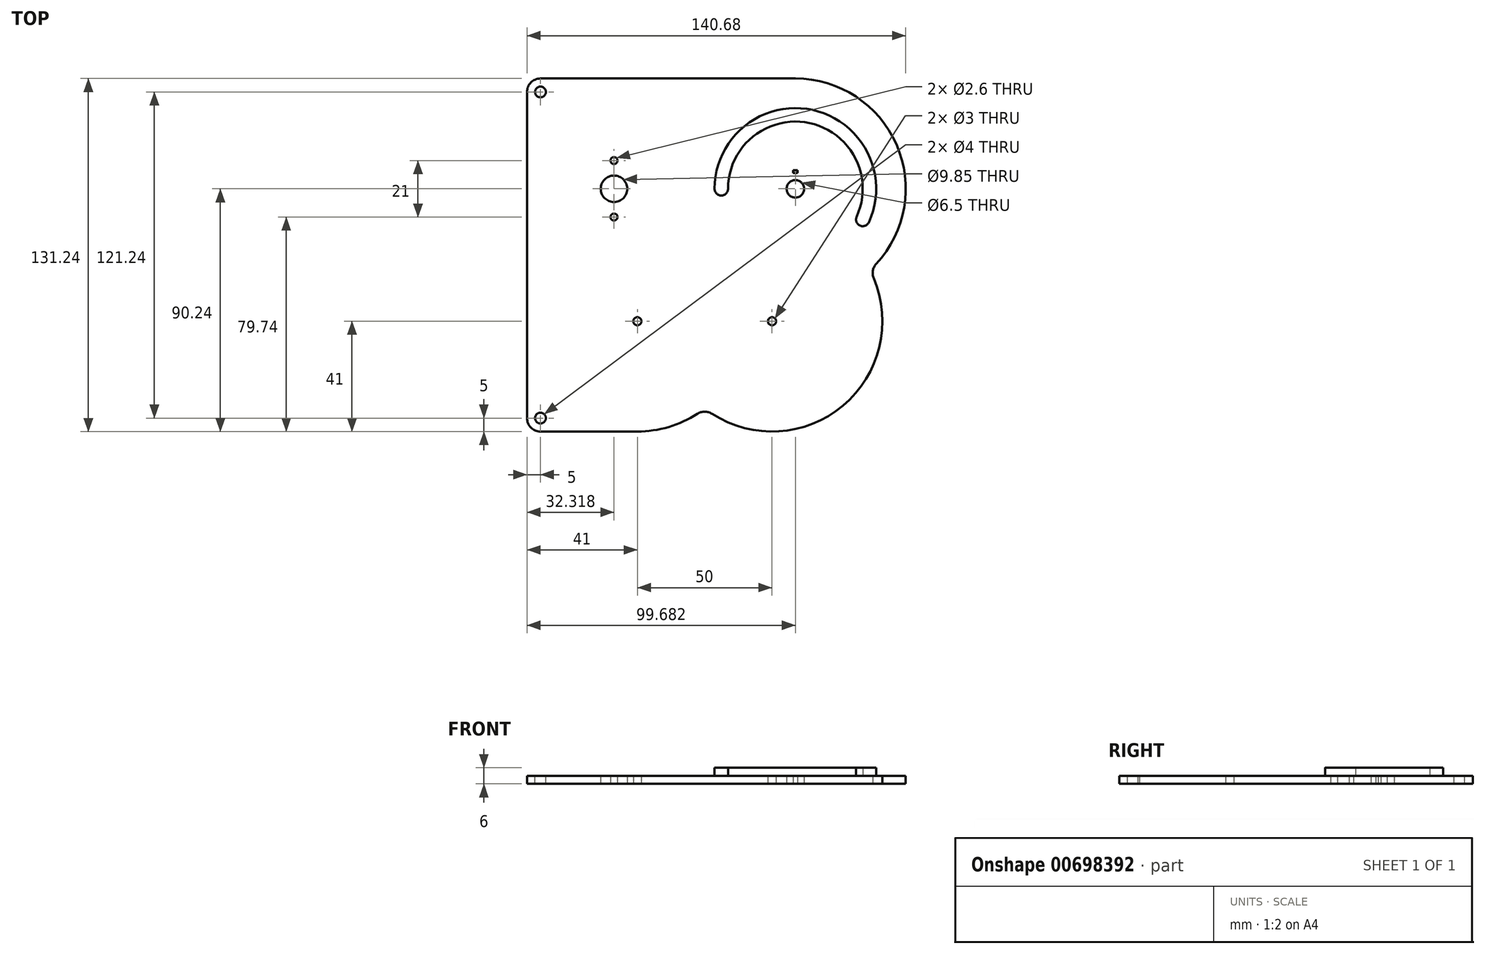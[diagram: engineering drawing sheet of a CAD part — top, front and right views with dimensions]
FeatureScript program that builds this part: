
annotation { "Feature Type Name" : "Feature", "Feature Type Description" : "" }
export const myFeature = defineFeature(function(context is Context, id is Id, definition is map)
    precondition{}
    {
        {
            assignVariable(context, id + "F0", {"name" : "thickness", "anyValue" : 3 * mm});
        }
        {
            assignVariable(context, id + "F1", {"name" : "kerf", "anyValue" : .3});
        }
        {
            assignVariable(context, id + "F2", {"name" : "diaIntermediate", "anyValue" : 3});
        }
        {
            var Q0;
            Q0=qCreatedBy(makeId("Top.planeOp"),FACE);
            var sketch = newSketch(context, id + "F3", { "sketchPlane" : qUnion([Q0])});
            skLineSegment(sketch, "E0.bottom", {"start": v(74.68, 65.62) * mm, "end": v(-66, 65.62) * mm});
            skLineSegment(sketch, "E0.top", {"start": v(74.68, -65.62) * mm, "end": v(-66, -65.62) * mm});
            skLineSegment(sketch, "E0.left", {"start": v(74.68, 65.62) * mm, "end": v(74.68, -65.62) * mm});
            skLineSegment(sketch, "E0.right", {"start": v(-66, 65.62) * mm, "end": v(-66, -65.62) * mm});
            skPoint(sketch, "E0.middle", {"position": v(0, 0) * mm});
            skPoint(sketch, "E1", {"position": v(-33.68, 24.62) * mm});
            skPoint(sketch, "E2", {"position": v(33.68, 24.62) * mm});
            skLineSegment(sketch, "E3", {"start": v(-33.68, 35.12) * mm, "end": v(-33.68, 14.12) * mm, "construction": true});
            skPoint(sketch, "E4", {"position": v(-33.68, 35.12) * mm});
            skPoint(sketch, "E5", {"position": v(-33.68, 14.12) * mm});
            skLineSegment(sketch, "E6.bottom", {"start": v(32.88, 31.5) * mm, "end": v(34.48, 31.5) * mm});
            skLineSegment(sketch, "E6.top", {"start": v(32.88, 30.5) * mm, "end": v(34.48, 30.5) * mm});
            skLineSegment(sketch, "E6.left", {"start": v(32.88, 31.5) * mm, "end": v(32.88, 30.5) * mm});
            skLineSegment(sketch, "E6.right", {"start": v(34.48, 31.5) * mm, "end": v(34.48, 30.5) * mm});
            skPoint(sketch, "E6.middle", {"position": v(33.68, 31) * mm});
            skLineSegment(sketch, "E7", {"start": v(33.68, 31) * mm, "end": v(33.68, 24.62) * mm, "construction": true});
            skLineSegment(sketch, "E8", {"start": v(-33.68, 24.62) * mm, "end": v(-25, -24.62) * mm, "construction": true});
            skLineSegment(sketch, "E9", {"start": v(-25, -24.62) * mm, "end": v(25, -24.62) * mm, "construction": true});
            skLineSegment(sketch, "E10", {"start": v(25, -24.62) * mm, "end": v(33.68, 24.62) * mm, "construction": true});
            skPoint(sketch, "E11", {"position": v(0, -24.62) * mm});
            skPoint(sketch, "E12", {"position": v(29.34, 0) * mm});
            skSolve(sketch);
        }
        {
            var Q0;
            Q0 = qSketchRegion(id + "F3", true);
            extrude(context, id + "F4", {"entities" : qUnion([Q0]), "depth" : getVariable(context, 'thickness'), "offsetDistance" : 25 * mm});
        }
        {
            var Q0;
            Q0=sQuery(id+"F3.wireOp",VERTEX,"E1");
            var Q1;
            Q1=makeQuery(id+"F4.opExtrude","SWEPT_BODY",BODY,{"disambiguationData":[OSD([sQuery(id+"F3.wireOp",EDGE,"E0.bottom"),sQuery(id+"F3.wireOp",EDGE,"E0.top"),sQuery(id+"F3.wireOp",EDGE,"E0.left"),sQuery(id+"F3.wireOp",EDGE,"E0.right"),sQuery(id+"F3.wireOp",EDGE,"E6.bottom"),sQuery(id+"F3.wireOp",EDGE,"E6.top"),sQuery(id+"F3.wireOp",EDGE,"E6.left"),sQuery(id+"F3.wireOp",EDGE,"E6.right")])]});
            hole(context, id + "F5", {"style" : HoleStyle.SIMPLE, "endStyle" : HoleEndStyle.THROUGH, "oppositeDirection" : true, "holeDiameter" : (4.92 * 2) * mm, "majorDiameter" : 5 * mm, "isTappedThrough" : true, "tappedDepth" : 12 * mm, "tapClearance" : 3, "locations" : qUnion([Q0]), "scope" : qUnion([Q1])});
        }
        {
            var Q0;
            Q0=sQuery(id+"F3.wireOp",VERTEX,"E2");
            var Q1;
            Q1=makeQuery(id+"F4.opExtrude","SWEPT_BODY",BODY,{"disambiguationData":[OSD([sQuery(id+"F3.wireOp",EDGE,"E0.bottom"),sQuery(id+"F3.wireOp",EDGE,"E0.top"),sQuery(id+"F3.wireOp",EDGE,"E0.left"),sQuery(id+"F3.wireOp",EDGE,"E0.right")])]});
            hole(context, id + "F6", {"style" : HoleStyle.SIMPLE, "endStyle" : HoleEndStyle.THROUGH, "oppositeDirection" : true, "holeDiameter" : (6.8 - getVariable(context, 'kerf')) * mm, "majorDiameter" : 5 * mm, "isTappedThrough" : true, "tappedDepth" : 12 * mm, "tapClearance" : 3, "locations" : qUnion([Q0]), "scope" : qUnion([Q1])});
        }
        {
            var Q0;
            Q0=sQuery(id+"F3.wireOp",VERTEX,"E5");
            var Q1;
            Q1=sQuery(id+"F3.wireOp",VERTEX,"E4");
            var Q2;
            Q2=makeQuery(id+"F4.opExtrude","SWEPT_BODY",BODY,{"disambiguationData":[OSD([sQuery(id+"F3.wireOp",EDGE,"E0.bottom"),sQuery(id+"F3.wireOp",EDGE,"E0.top"),sQuery(id+"F3.wireOp",EDGE,"E0.left"),sQuery(id+"F3.wireOp",EDGE,"E0.right"),sQuery(id+"F3.wireOp",EDGE,"E6.bottom"),sQuery(id+"F3.wireOp",EDGE,"E6.top"),sQuery(id+"F3.wireOp",EDGE,"E6.left"),sQuery(id+"F3.wireOp",EDGE,"E6.right")])]});
            hole(context, id + "F7", {"style" : HoleStyle.SIMPLE, "endStyle" : HoleEndStyle.THROUGH, "oppositeDirection" : true, "holeDiameter" : 2.6 * mm, "majorDiameter" : 5 * mm, "isTappedThrough" : true, "tappedDepth" : 12 * mm, "tapClearance" : 3, "locations" : qUnion([Q0, Q1]), "scope" : qUnion([Q2])});
        }
        {
            var Q0;
            Q0=sQuery(id+"F3.wireOp",VERTEX,"E8.end");
            var Q1;
            Q1=sQuery(id+"F3.wireOp",VERTEX,"E9.end");
            var Q2;
            Q2=makeQuery(id+"F4.opExtrude","SWEPT_BODY",BODY,{"disambiguationData":[OSD([sQuery(id+"F3.wireOp",EDGE,"E0.bottom"),sQuery(id+"F3.wireOp",EDGE,"E0.top"),sQuery(id+"F3.wireOp",EDGE,"E0.left"),sQuery(id+"F3.wireOp",EDGE,"E0.right"),sQuery(id+"F3.wireOp",EDGE,"E6.bottom"),sQuery(id+"F3.wireOp",EDGE,"E6.top"),sQuery(id+"F3.wireOp",EDGE,"E6.left"),sQuery(id+"F3.wireOp",EDGE,"E6.right")])]});
            hole(context, id + "F8", {"style" : HoleStyle.SIMPLE, "endStyle" : HoleEndStyle.THROUGH, "oppositeDirection" : true, "holeDiameter" : (getVariable(context, 'diaIntermediate')) * mm, "majorDiameter" : 5 * mm, "isTappedThrough" : true, "tappedDepth" : 12 * mm, "tapClearance" : 3, "locations" : qUnion([Q0, Q1]), "scope" : qUnion([Q2])});
        }
        {
            var Q0;
            Q0=makeQuery(id+"F4.opExtrude","CAP_FACE",FACE,{"disambiguationData":[OSD([sQuery(id+"F3.wireOp",EDGE,"E0.bottom"),sQuery(id+"F3.wireOp",EDGE,"E0.top"),sQuery(id+"F3.wireOp",EDGE,"E0.left"),sQuery(id+"F3.wireOp",EDGE,"E0.right"),sQuery(id+"F3.wireOp",EDGE,"E6.bottom"),sQuery(id+"F3.wireOp",EDGE,"E6.top"),sQuery(id+"F3.wireOp",EDGE,"E6.left"),sQuery(id+"F3.wireOp",EDGE,"E6.right")])],"isStart":false});
            var sketch = newSketch(context, id + "F9", { "sketchPlane" : qUnion([Q0])});
            skArc(sketch, "E13", {"start": v(-25, -65.62) * mm, "mid": v(-11.8, -63.44) * mm, "end": v(0, -57.12) * mm});
            skArc(sketch, "E14", {"start": v(0, -57.12) * mm, "mid": v(51.35, -56.03) * mm, "end": v(61.34, -5.64) * mm});
            skArc(sketch, "E15", {"start": v(61.34, -5.64) * mm, "mid": v(71.9, 39.46) * mm, "end": v(33.68, 65.62) * mm});
            skLineSegment(sketch, "E16", {"start": v(33.68, 65.62) * mm, "end": v(74.68, 65.62) * mm});
            skLineSegment(sketch, "E17", {"start": v(74.68, 65.62) * mm, "end": v(74.68, -65.62) * mm});
            skLineSegment(sketch, "E18", {"start": v(74.68, -65.62) * mm, "end": v(-25, -65.62) * mm});
            skCircle(sketch, "E19", {"center": v(-61, -60.62) * mm, "radius": 2 * mm});
            skCircle(sketch, "E20", {"center": v(-61, 60.62) * mm, "radius": 2 * mm});
            skLineSegment(sketch, "E21", {"start": v(-61, 60.62) * mm, "end": v(-61, -60.62) * mm, "construction": true});
            skPoint(sketch, "E22", {"position": v(-61, 0) * mm});
            skSolve(sketch);
        }
        {
            var Q0;
            Q0 = qSketchRegion(id + "F9", true);
            extrude(context, id + "F10", {"entities" : qUnion([Q0]), "operationType" : NewBodyOperationType.REMOVE, "endBound" : BoundingType.THROUGH_ALL, "oppositeDirection" : true, "depth" : 25 * mm, "offsetDistance" : 25 * mm});
        }
        {
            var Q0;
            Q0=makeQuery(id+"F10.boolean.opBoolean","COPY",EDGE,{"derivedFrom":makeQuery(id+"F10.opExtrude","SWEPT_EDGE",EDGE,{"disambiguationData":[OSD([sQuery(id+"F9.wireOp",EDGE,"E13"),sQuery(id+"F9.wireOp",EDGE,"E14")])]})});
            var Q1;
            Q1=makeQuery(id+"F10.boolean.opBoolean","COPY",EDGE,{"derivedFrom":makeQuery(id+"F10.opExtrude","SWEPT_EDGE",EDGE,{"disambiguationData":[OSD([sQuery(id+"F9.wireOp",EDGE,"E14"),sQuery(id+"F9.wireOp",EDGE,"E15")])]})});
            var Q2;
            Q2=makeQuery(id+"F4.opExtrude","SWEPT_EDGE",EDGE,{"disambiguationData":[OSD([sQuery(id+"F3.wireOp",EDGE,"E0.top"),sQuery(id+"F3.wireOp",EDGE,"E0.right")])]});
            var Q3;
            Q3=makeQuery(id+"F4.opExtrude","SWEPT_EDGE",EDGE,{"disambiguationData":[OSD([sQuery(id+"F3.wireOp",EDGE,"E0.bottom"),sQuery(id+"F3.wireOp",EDGE,"E0.right")])]});
            fillet(context, id + "F11", {"entities" : qUnion([Q0, Q1, Q2, Q3]), "radius" : 5 * mm, "tangentPropagation" : true, "allowEdgeOverflow" : false});
        }
        {
            var Q0;
            Q0=makeQuery(id+"F4.opExtrude","CAP_FACE",FACE,{"disambiguationData":[OSD([sQuery(id+"F3.wireOp",EDGE,"E0.bottom"),sQuery(id+"F3.wireOp",EDGE,"E0.top"),sQuery(id+"F3.wireOp",EDGE,"E0.left"),sQuery(id+"F3.wireOp",EDGE,"E0.right"),sQuery(id+"F3.wireOp",EDGE,"E6.bottom"),sQuery(id+"F3.wireOp",EDGE,"E6.top"),sQuery(id+"F3.wireOp",EDGE,"E6.left"),sQuery(id+"F3.wireOp",EDGE,"E6.right")])],"isStart":false});
            var sketch = newSketch(context, id + "F12", { "sketchPlane" : qUnion([Q0])});
            skArc(sketch, "E23", {"start": v(8.68, 24.62) * mm, "mid": v(38.98, 49.05) * mm, "end": v(56.44, 14.26) * mm});
            skCircle(sketch, "E24", {"center": v(25, -24.62) * mm, "radius": 40 * mm, "construction": true});
            skArc(sketch, "E25.0", {"start": v(3.68, 24.62) * mm, "mid": v(40.04, 53.94) * mm, "end": v(60.99, 12.2) * mm});
            skArc(sketch, "E26", {"start": v(3.68, 24.62) * mm, "mid": v(6.18, 22.12) * mm, "end": v(8.68, 24.62) * mm});
            skArc(sketch, "E27", {"start": v(56.44, 14.26) * mm, "mid": v(57.67, 10.95) * mm, "end": v(60.99, 12.2) * mm});
            skSolve(sketch);
        }
        {
            var Q0;
            Q0 = qSketchRegion(id + "F12", true);
            extrude(context, id + "F13", {"entities" : qUnion([Q0]), "depth" : getVariable(context, 'thickness'), "offsetDistance" : 25 * mm});
        }
    });
